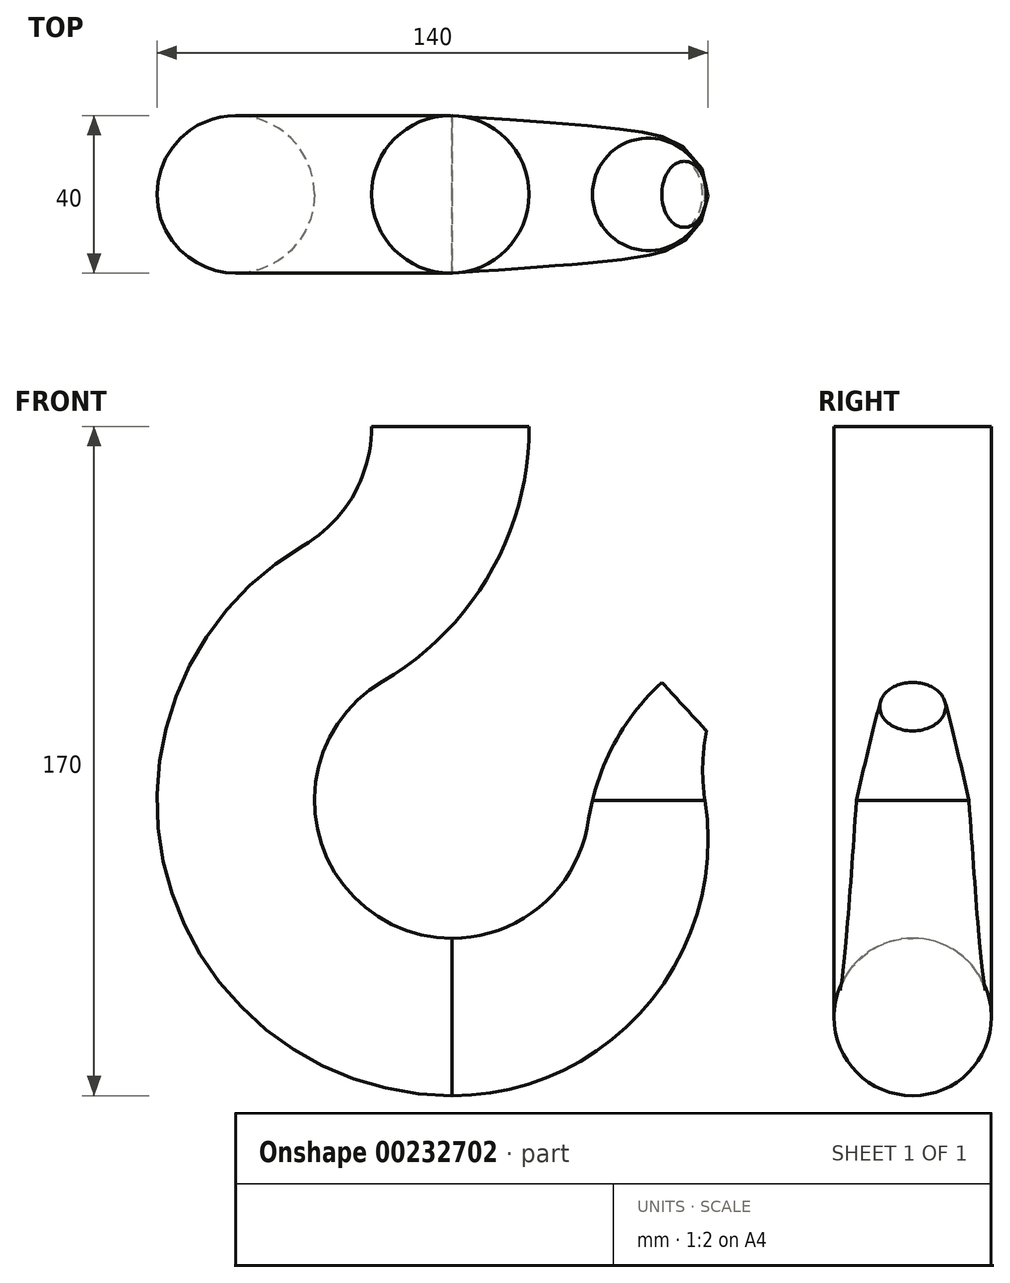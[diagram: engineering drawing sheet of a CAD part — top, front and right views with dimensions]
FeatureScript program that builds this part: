
annotation { "Feature Type Name" : "Feature", "Feature Type Description" : "" }
export const myFeature = defineFeature(function(context is Context, id is Id, definition is map)
    precondition{}
    {
        {
            var Q0;
            Q0=qCreatedBy(makeId("Front.planeOp"),FACE);
            var sketch = newSketch(context, id + "F0", { "sketchPlane" : qUnion([Q0])});
            skArc(sketch, "E0", {"start": v(-37.8, 64.77) * mm, "mid": v(-25.1, 77.57) * mm, "end": v(-20.45, 95) * mm, "construction": true});
            skArc(sketch, "E1", {"start": v(-17.64, 30.23) * mm, "mid": v(9.59, 57.65) * mm, "end": v(19.55, 95) * mm, "construction": true});
            skArc(sketch, "E2", {"start": v(-37.8, 64.77) * mm, "mid": v(-72.4, -19.58) * mm, "end": v(0, -75) * mm, "construction": true});
            skArc(sketch, "E3", {"start": v(-17.64, 30.23) * mm, "mid": v(-19.64, -28.97) * mm, "end": v(34.61, -5.2) * mm, "construction": true});
            skArc(sketch, "E4.0", {"start": v(-27.73, 47.5) * mm, "mid": v(-53.1, -14.36) * mm, "end": v(0, -55) * mm});
            skArc(sketch, "E5.0", {"start": v(-27.73, 47.5) * mm, "mid": v(-7.76, 67.61) * mm, "end": v(-0.45, 95) * mm});
            skArc(sketch, "E6", {"start": v(0, -75) * mm, "mid": v(49.37, -52.28) * mm, "end": v(64.23, 0) * mm, "construction": true});
            skPoint(sketch, "E7.orphan", {"position": v(0, -35) * mm});
            skArc(sketch, "E8", {"start": v(34.61, -5.2) * mm, "mid": v(40.94, 14) * mm, "end": v(53.27, 30) * mm, "construction": true});
            skArc(sketch, "E9", {"start": v(64.23, 0) * mm, "mid": v(63.64, 8.86) * mm, "end": v(64.64, 17.68) * mm, "construction": true});
            skLineSegment(sketch, "E10", {"start": v(53.27, 30) * mm, "end": v(64.64, 17.68) * mm, "construction": true});
            skPoint(sketch, "E11.orphan", {"position": v(34.36, 6.67) * mm});
            skLineSegment(sketch, "E12", {"start": v(53.27, 30) * mm, "end": v(63.53, 39.46) * mm, "construction": true});
            skSolve(sketch);
        }
        {
            var Q0;
            Q0=sQuery(id+"F0.wireOp",VERTEX,"E5.0.end");
            var Q1;
            Q1=qCreatedBy(makeId("Top.planeOp"),FACE);
            cPlane(context, id + "F1", {"entities" : qUnion([Q0, Q1]), "cplaneType" : CPlaneType.PLANE_POINT, "offset" : 25 * mm, "width" : 150 * mm, "height" : 150 * mm});
        }
        {
            var Q0;
            Q0=qCreatedBy(id+"F1.planeOp",FACE);
            var sketch = newSketch(context, id + "F2", { "sketchPlane" : qUnion([Q0])});
            skCircle(sketch, "E13", {"center": v(-0.45, 0) * mm, "radius": 20 * mm});
            skSolve(sketch);
        }
        {
            var Q0;
            Q0=qCreatedBy(makeId("Front.planeOp"),FACE);
            var sketch = newSketch(context, id + "F3", { "sketchPlane" : qUnion([Q0])});
            skArc(sketch, "E14.0", {"start": v(-27.73, 47.5) * mm, "mid": v(-53.1, -14.36) * mm, "end": v(0, -55) * mm});
            skArc(sketch, "E14.1", {"start": v(-27.73, 47.5) * mm, "mid": v(-7.76, 67.61) * mm, "end": v(-0.45, 95) * mm});
            skSolve(sketch);
        }
        {
            var Q0;
            Q0=qCreatedBy(makeId("Right.planeOp"),FACE);
            var sketch = newSketch(context, id + "F4", { "sketchPlane" : qUnion([Q0])});
            skCircle(sketch, "E15.0.0", {"center": v(0, -55) * mm, "radius": 20 * mm});
            skSolve(sketch);
        }
        {
            var Q0;
            Q0=qCreatedBy(makeId("Top.planeOp"),FACE);
            var sketch = newSketch(context, id + "F5", { "sketchPlane" : qUnion([Q0])});
            skLineSegment(sketch, "E16.0", {"start": v(35.63, 0) * mm, "end": v(53.27, 0) * mm, "construction": true});
            skPoint(sketch, "E17.0", {"position": v(64.23, 0) * mm});
            skCircle(sketch, "E18", {"center": v(49.93, 0) * mm, "radius": 14.3 * mm});
            skSolve(sketch);
        }
        {
            var Q0;
            Q0=qCreatedBy(makeId("Front.planeOp"),FACE);
            var sketch = newSketch(context, id + "F6", { "sketchPlane" : qUnion([Q0])});
            skArc(sketch, "E19.1", {"start": v(0, -35) * mm, "mid": v(22.84, -26.52) * mm, "end": v(34.61, -5.2) * mm});
            skLineSegment(sketch, "E20.0.0", {"start": v(0, -35) * mm, "end": v(0, -75) * mm, "construction": true});
            skPoint(sketch, "E21.orphan", {"position": v(-17.64, 30.23) * mm});
            skArc(sketch, "E22.0", {"start": v(34.61, -5.2) * mm, "mid": v(35.06, -2.59) * mm, "end": v(35.63, 0) * mm});
            skLineSegment(sketch, "E23.0", {"start": v(35.63, 0) * mm, "end": v(64.23, 0) * mm, "construction": true});
            skPoint(sketch, "E24.orphan", {"position": v(53.27, 30) * mm});
            skPoint(sketch, "E19.0.end.orphan", {"position": v(64.23, 0) * mm});
            skPoint(sketch, "E19.0.start.orphan", {"position": v(0, -75) * mm});
            skSolve(sketch);
        }
        {
            var Q0;
            Q0=qCreatedBy(makeId("Front.planeOp"),FACE);
            var sketch = newSketch(context, id + "F7", { "sketchPlane" : qUnion([Q0])});
            skArc(sketch, "E25.0", {"start": v(0, -75) * mm, "mid": v(49.37, -52.28) * mm, "end": v(64.23, 0) * mm});
            skSolve(sketch);
        }
        {
            var Q0;
            Q0=makeQuery(id+"F2.imprint","IMPRINT",FACE,{"disambiguationData":[TD([[makeQuery(id+"F2.imprint","IMPRINT",EDGE,{"derivedFrom":sQuery(id+"F2.wireOp",EDGE,"E13")}),1.0]])]});
            var Q1;
            Q1=sQuery(id+"F3.wireOp",EDGE,"E14.1");
            var Q2;
            Q2=sQuery(id+"F3.wireOp",EDGE,"E14.0");
            sweep(context, id + "F8", {"profiles" : qUnion([Q0]), "path" : qUnion([Q1, Q2])});
        }
        {
            var Q0;
            Q0=makeQuery(id+"F4.imprint","IMPRINT",FACE,{"disambiguationData":[TD([[makeQuery(id+"F4.imprint","IMPRINT",EDGE,{"derivedFrom":sQuery(id+"F4.wireOp",EDGE,"E15.0.0")}),1.0]])]});
            var Q1;
            Q1=makeQuery(id+"F5.imprint","IMPRINT",FACE,{"disambiguationData":[TD([[makeQuery(id+"F5.imprint","IMPRINT",EDGE,{"derivedFrom":sQuery(id+"F5.wireOp",EDGE,"E18")}),1.0]])]});
            var Q2;
            Q2 = qConstructionFilter(qBodyType(qCreatedBy(id + "F6" ,EDGE), BodyType.WIRE), ConstructionObject.NO);
            var Q3;
            Q3 = qConstructionFilter(qBodyType(qCreatedBy(id + "F7" ,EDGE), BodyType.WIRE), ConstructionObject.NO);
            loft(context, id + "F9", {"operationType" : NewBodyOperationType.ADD, "addGuides" : true, "sheetProfilesArray" : [{ "sheetProfileEntities" : qUnion([Q0]) }, { "sheetProfileEntities" : qUnion([Q1]) }], "guidesArray" : [{ "guideEntities" : qUnion([Q2]), "guideDerivativeType" : LoftGuideDerivativeType.DEFAULT, "guideDerivativeMagnitude" : 1 }, { "guideEntities" : qUnion([Q3]), "guideDerivativeType" : LoftGuideDerivativeType.DEFAULT, "guideDerivativeMagnitude" : 1 }]});
        }
        {
            var Q0;
            Q0=sQuery(id+"F0.wireOp",EDGE,"E10");
            cPlane(context, id + "F10", {"entities" : qUnion([Q0]), "cplaneType" : CPlaneType.LINE_ANGLE, "offset" : 25 * mm, "angle" : 0 * degree, "width" : 150 * mm, "height" : 150 * mm});
        }
        {
            var Q0;
            Q0=qCreatedBy(id+"F10.planeOp",FACE);
            var sketch = newSketch(context, id + "F11", { "sketchPlane" : qUnion([Q0])});
            skCircle(sketch, "E26", {"center": v(0, -22.44) * mm, "radius": 8.38 * mm});
            skSolve(sketch);
        }
        {
            var Q0;
            Q0=qCreatedBy(makeId("Front.planeOp"),FACE);
            var sketch = newSketch(context, id + "F12", { "sketchPlane" : qUnion([Q0])});
            skArc(sketch, "E27.0", {"start": v(35.63, 0) * mm, "mid": v(42.23, 16.3) * mm, "end": v(53.27, 30) * mm});
            skPoint(sketch, "E28", {"position": v(35.63, 0) * mm});
            skPoint(sketch, "E29.orphan", {"position": v(34.61, -5.2) * mm});
            skSolve(sketch);
        }
        {
            var Q0;
            Q0=qCreatedBy(makeId("Front.planeOp"),FACE);
            var sketch = newSketch(context, id + "F13", { "sketchPlane" : qUnion([Q0])});
            skArc(sketch, "E30.0", {"start": v(64.23, 0) * mm, "mid": v(63.64, 8.86) * mm, "end": v(64.64, 17.68) * mm});
            skSolve(sketch);
        }
        {
            var Q0;
            Q0=qCreatedBy(makeId("Top.planeOp"),FACE);
            var sketch = newSketch(context, id + "F14", { "sketchPlane" : qUnion([Q0])});
            skCircle(sketch, "E31", {"center": v(49.93, 0) * mm, "radius": 14.3 * mm});
            skSolve(sketch);
        }
        {
            var Q0;
            Q0 = qSketchRegion(id + "F14", true);
            var Q1;
            Q1=makeQuery(id+"F11.imprint","IMPRINT",FACE,{"disambiguationData":[TD([[makeQuery(id+"F11.imprint","IMPRINT",EDGE,{"derivedFrom":sQuery(id+"F11.wireOp",EDGE,"E26")}),1.0]])]});
            var Q2;
            Q2=sQuery(id+"F12.wireOp",EDGE,"E27.0");
            var Q3;
            Q3=sQuery(id+"F13.wireOp",EDGE,"E30.0");
            loft(context, id + "F15", {"operationType" : NewBodyOperationType.ADD, "addGuides" : true, "sheetProfilesArray" : [{ "sheetProfileEntities" : qUnion([Q0]) }, { "sheetProfileEntities" : qUnion([Q1]) }], "guidesArray" : [{ "guideEntities" : qUnion([Q2]), "guideDerivativeType" : LoftGuideDerivativeType.DEFAULT, "guideDerivativeMagnitude" : 1 }, { "guideEntities" : qUnion([Q3]), "guideDerivativeType" : LoftGuideDerivativeType.DEFAULT, "guideDerivativeMagnitude" : 1 }]});
        }
    });
